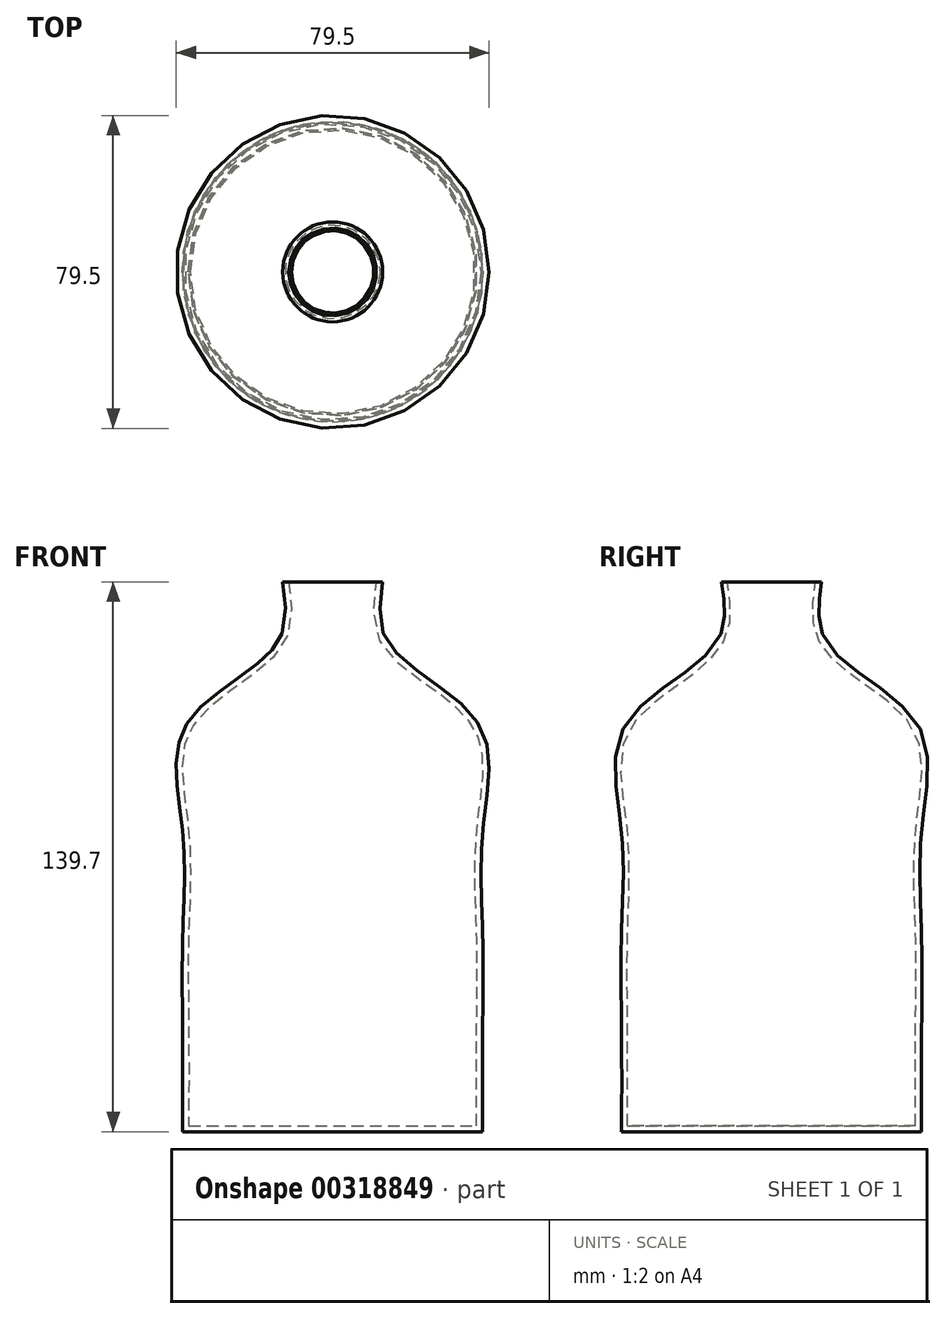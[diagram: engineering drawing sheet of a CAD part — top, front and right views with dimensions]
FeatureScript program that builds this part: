
annotation { "Feature Type Name" : "Feature", "Feature Type Description" : "" }
export const myFeature = defineFeature(function(context is Context, id is Id, definition is map)
    precondition{}
    {
        {
            var Q0;
            Q0=qCreatedBy(makeId("Top.planeOp"),FACE);
            var sketch = newSketch(context, id + "F0", { "sketchPlane" : qUnion([Q0])});
            skCircle(sketch, "E0", {"center": v(0, 0) * mm, "radius": 38.1 * mm});
            skSolve(sketch);
        }
        {
            var Q0;
            Q0=qCreatedBy(makeId("Top.planeOp"),FACE);
            cPlane(context, id + "F1", {"entities" : qUnion([Q0]), "cplaneType" : CPlaneType.OFFSET, "offset" : 25.4 * mm, "width" : 152.4 * mm, "height" : 152.4 * mm});
        }
        {
            var Q0;
            Q0=qCreatedBy(id+"F1.planeOp",FACE);
            var sketch = newSketch(context, id + "F2", { "sketchPlane" : qUnion([Q0])});
            skCircle(sketch, "E1", {"center": v(0, 0) * mm, "radius": 38.1 * mm});
            skSolve(sketch);
        }
        {
            var Q0;
            Q0=qCreatedBy(id+"F1.planeOp",FACE);
            cPlane(context, id + "F3", {"entities" : qUnion([Q0]), "cplaneType" : CPlaneType.OFFSET, "offset" : 25.4 * mm, "width" : 152.4 * mm, "height" : 152.4 * mm});
        }
        {
            var Q0;
            Q0=qCreatedBy(id+"F3.planeOp",FACE);
            var sketch = newSketch(context, id + "F4", { "sketchPlane" : qUnion([Q0])});
            skCircle(sketch, "E2", {"center": v(0, 0) * mm, "radius": 38.1 * mm});
            skSolve(sketch);
        }
        {
            var Q0;
            Q0=qCreatedBy(id+"F3.planeOp",FACE);
            cPlane(context, id + "F5", {"entities" : qUnion([Q0]), "cplaneType" : CPlaneType.OFFSET, "offset" : 25.4 * mm, "width" : 152.4 * mm, "height" : 152.4 * mm});
        }
        {
            var Q0;
            Q0=qCreatedBy(id+"F5.planeOp",FACE);
            var sketch = newSketch(context, id + "F6", { "sketchPlane" : qUnion([Q0])});
            skCircle(sketch, "E3", {"center": v(0, 0) * mm, "radius": 38.1 * mm});
            skSolve(sketch);
        }
        {
            var Q0;
            Q0=qCreatedBy(id+"F5.planeOp",FACE);
            cPlane(context, id + "F7", {"entities" : qUnion([Q0]), "cplaneType" : CPlaneType.OFFSET, "offset" : 25.4 * mm, "width" : 152.4 * mm, "height" : 152.4 * mm});
        }
        {
            var Q0;
            Q0=qCreatedBy(id+"F7.planeOp",FACE);
            var sketch = newSketch(context, id + "F8", { "sketchPlane" : qUnion([Q0])});
            skCircle(sketch, "E4", {"center": v(0, 0) * mm, "radius": 38.1 * mm});
            skSolve(sketch);
        }
        {
            var Q0;
            Q0=qCreatedBy(id+"F7.planeOp",FACE);
            cPlane(context, id + "F9", {"entities" : qUnion([Q0]), "cplaneType" : CPlaneType.OFFSET, "offset" : 12.7 * mm, "width" : 152.4 * mm, "height" : 152.4 * mm});
        }
        {
            var Q0;
            Q0=qCreatedBy(id+"F9.planeOp",FACE);
            var sketch = newSketch(context, id + "F10", { "sketchPlane" : qUnion([Q0])});
            skCircle(sketch, "E5", {"center": v(0, 0) * mm, "radius": 25.4 * mm});
            skSolve(sketch);
        }
        {
            var Q0;
            Q0=qCreatedBy(id+"F9.planeOp",FACE);
            cPlane(context, id + "F11", {"entities" : qUnion([Q0]), "cplaneType" : CPlaneType.OFFSET, "offset" : 12.7 * mm, "width" : 152.4 * mm, "height" : 152.4 * mm});
        }
        {
            var Q0;
            Q0=qCreatedBy(id+"F11.planeOp",FACE);
            var sketch = newSketch(context, id + "F12", { "sketchPlane" : qUnion([Q0])});
            skCircle(sketch, "E6", {"center": v(0, 0) * mm, "radius": 12.7 * mm});
            skSolve(sketch);
        }
        {
            var Q0;
            Q0=qCreatedBy(id+"F11.planeOp",FACE);
            cPlane(context, id + "F13", {"entities" : qUnion([Q0]), "cplaneType" : CPlaneType.OFFSET, "offset" : 12.7 * mm, "width" : 152.4 * mm, "height" : 152.4 * mm});
        }
        {
            var Q0;
            Q0=qCreatedBy(id+"F13.planeOp",FACE);
            var sketch = newSketch(context, id + "F14", { "sketchPlane" : qUnion([Q0])});
            skCircle(sketch, "E7", {"center": v(0, 0) * mm, "radius": 12.7 * mm});
            skSolve(sketch);
        }
        {
            var Q0;
            Q0=makeQuery(id+"F14.imprint","IMPRINT",FACE,{"disambiguationData":[TD([[makeQuery(id+"F14.imprint","IMPRINT",EDGE,{"derivedFrom":sQuery(id+"F14.wireOp",EDGE,"E7")}),1.0]])]});
            var Q1;
            Q1=makeQuery(id+"F12.imprint","IMPRINT",FACE,{"disambiguationData":[TD([[makeQuery(id+"F12.imprint","IMPRINT",EDGE,{"derivedFrom":sQuery(id+"F12.wireOp",EDGE,"E6")}),1.0]])]});
            var Q2;
            Q2=makeQuery(id+"F10.imprint","IMPRINT",FACE,{"disambiguationData":[TD([[makeQuery(id+"F10.imprint","IMPRINT",EDGE,{"derivedFrom":sQuery(id+"F10.wireOp",EDGE,"E5")}),1.0]])]});
            var Q3;
            Q3=makeQuery(id+"F8.imprint","IMPRINT",FACE,{"disambiguationData":[TD([[makeQuery(id+"F8.imprint","IMPRINT",EDGE,{"derivedFrom":sQuery(id+"F8.wireOp",EDGE,"E4")}),1.0]])]});
            var Q4;
            Q4=makeQuery(id+"F6.imprint","IMPRINT",FACE,{"disambiguationData":[TD([[makeQuery(id+"F6.imprint","IMPRINT",EDGE,{"derivedFrom":sQuery(id+"F6.wireOp",EDGE,"E3")}),1.0]])]});
            var Q5;
            Q5=makeQuery(id+"F4.imprint","IMPRINT",FACE,{"disambiguationData":[TD([[makeQuery(id+"F4.imprint","IMPRINT",EDGE,{"derivedFrom":sQuery(id+"F4.wireOp",EDGE,"E2")}),1.0]])]});
            var Q6;
            Q6=makeQuery(id+"F2.imprint","IMPRINT",FACE,{"disambiguationData":[TD([[makeQuery(id+"F2.imprint","IMPRINT",EDGE,{"derivedFrom":sQuery(id+"F2.wireOp",EDGE,"E1")}),1.0]])]});
            var Q7;
            Q7=makeQuery(id+"F0.imprint","IMPRINT",FACE,{"disambiguationData":[TD([[makeQuery(id+"F0.imprint","IMPRINT",EDGE,{"derivedFrom":sQuery(id+"F0.wireOp",EDGE,"E0")}),1.0]])]});
            loft(context, id + "F15", {"sheetProfilesArray" : [{ "sheetProfileEntities" : qUnion([Q0]) }, { "sheetProfileEntities" : qUnion([Q1]) }, { "sheetProfileEntities" : qUnion([Q2]) }, { "sheetProfileEntities" : qUnion([Q3]) }, { "sheetProfileEntities" : qUnion([Q4]) }, { "sheetProfileEntities" : qUnion([Q5]) }, { "sheetProfileEntities" : qUnion([Q6]) }, { "sheetProfileEntities" : qUnion([Q7]) }]});
        }
        {
            var Q0;
            Q0=makeQuery(id+"F15.opLoft","CAP_FACE",FACE,{"disambiguationData":[OSD([makeQuery(id+"F14.imprint","IMPRINT",FACE,{"disambiguationData":[TD([[makeQuery(id+"F14.imprint","IMPRINT",EDGE,{"derivedFrom":sQuery(id+"F14.wireOp",EDGE,"E7")}),1.0]])]})])],"isStart":true});
            shell(context, id + "F16", {"entities" : qUnion([Q0]), "thickness" : 1.52 * mm});
        }
    });
